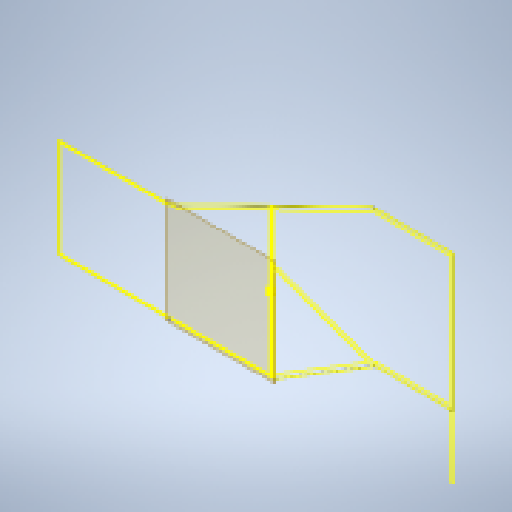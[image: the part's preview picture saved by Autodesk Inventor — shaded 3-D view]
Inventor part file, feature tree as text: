
AUTODESK INVENTOR PART (.ipt)
format: ipt  version: 2025 (Build 290162000, 162)  size: 143,360 bytes
history: native  units: in
note: dims shown in document units (in); Inventor stores cm internally (conversion verified against a paired STEP export)
features: other x19, reference x13, plane x1, sketch x1
ambient origin geometry x8: Origin, YZ Plane, XZ Plane, XY Plane, X Axis, Y Axis, Z Axis, Center Point
feature tree (34):
  plane  "Work Plane1"
  sketch  "Sketch1"  dims[d0=0.5in d1=0.0344in d2=0.5in d3=0.0344in]
  reference  "Reference1"
  reference  "Reference2"
  reference  "Reference3"
  reference  "Reference4"
  reference  "Reference5"
  reference  "Reference6"
  reference  "Reference7"
  reference  "Reference8"
  reference  "Reference9"
  reference  "Reference10"
  reference  "Reference11"
  reference  "Reference12"
  reference  "Reference13"
  other  "<userpath>\Documents\USCTigerBurn24\Tburn24\FullAssembly\FullAssembly.iam"
  other  "FullAssembly.iam"
  other  "layer1:1"
  other  "s58x2x4:1"
  other  "Assembly1:1"
  other  "6'x4x4:15"
  other  "16'x4x4:2"
  other  "6'x4x4:20"
  other  "s48'x2x4:1"
  other  "layer2:1"
  other  "s48x2x4a:2"
  other  "Head:1"
  other  "10'x2x4:4"
  other  "2x4x96:3"
  other  "10'x2x4:2"
  other  "8'x2x4:1"
  other  "12'x2x4:2"
  other  "12'x2x4:1"
  other  "s88x2x4:1"
